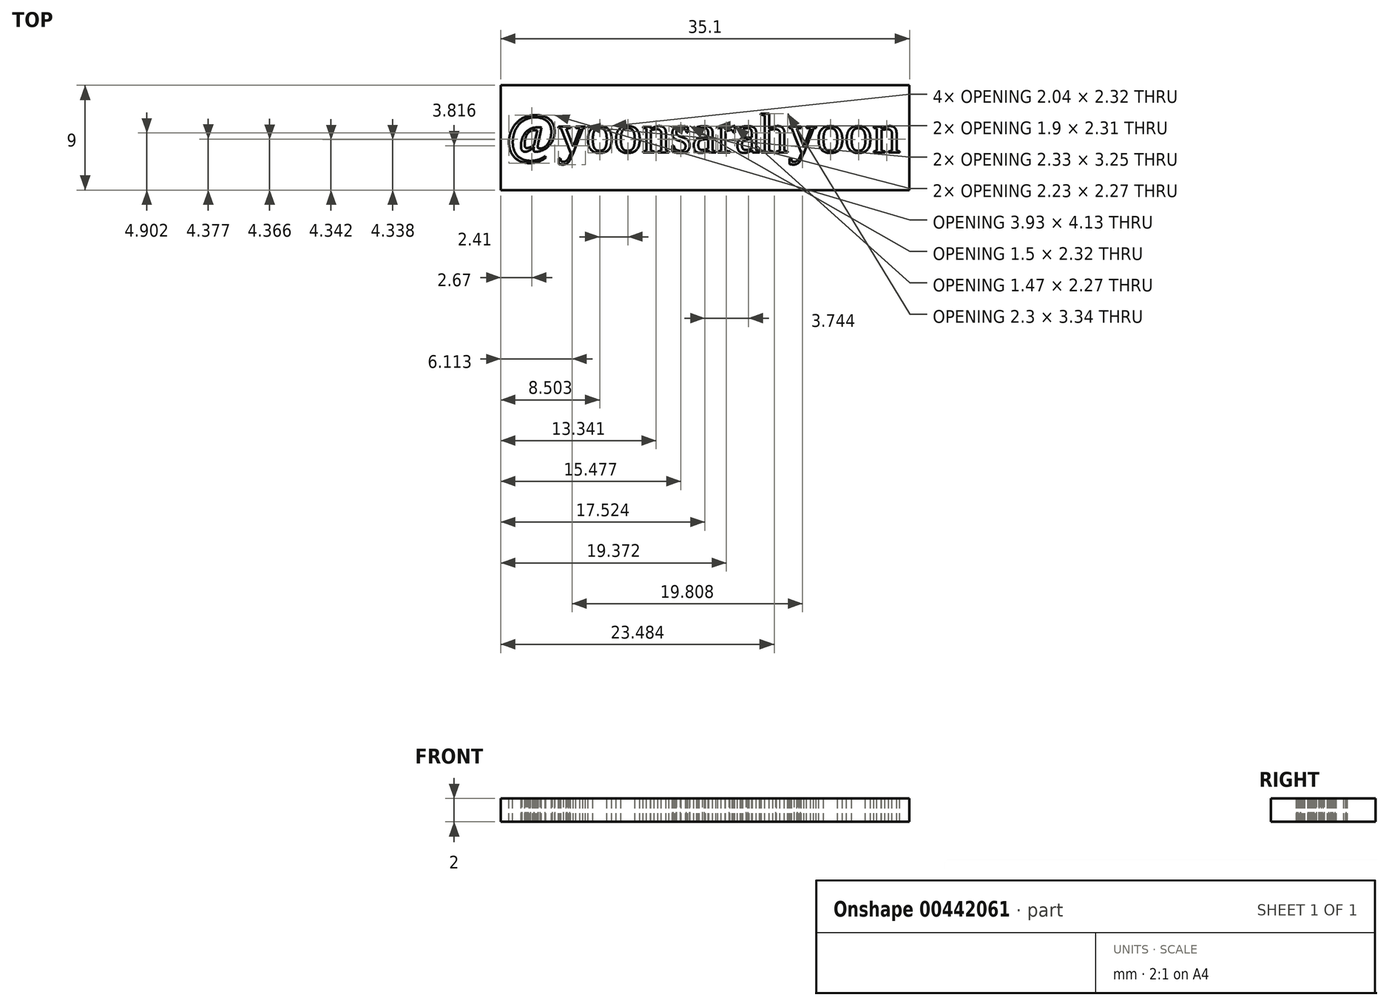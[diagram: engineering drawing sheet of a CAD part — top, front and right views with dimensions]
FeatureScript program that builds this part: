
annotation { "Feature Type Name" : "Feature", "Feature Type Description" : "" }
export const myFeature = defineFeature(function(context is Context, id is Id, definition is map)
    precondition{}
    {
        {
            var Q0;
            Q0=qCreatedBy(makeId("Top.planeOp"),FACE);
            var sketch = newSketch(context, id + "F0", { "sketchPlane" : qUnion([Q0])});
            skLineSegment(sketch, "E0.bottom", {"start": v(17.55, -4.5) * mm, "end": v(-17.55, -4.5) * mm});
            skLineSegment(sketch, "E0.top", {"start": v(17.55, 4.5) * mm, "end": v(-17.55, 4.5) * mm});
            skLineSegment(sketch, "E0.left", {"start": v(17.55, -4.5) * mm, "end": v(17.55, 4.5) * mm});
            skLineSegment(sketch, "E0.right", {"start": v(-17.55, -4.5) * mm, "end": v(-17.55, 4.5) * mm});
            skPoint(sketch, "E0.middle", {"position": v(0, 0) * mm});
            skSolve(sketch);
        }
        {
            var Q0;
            Q0=makeQuery(id+"F0.imprint","IMPRINT",FACE,{"disambiguationData":[TD([[makeQuery(id+"F0.imprint","IMPRINT",EDGE,{"derivedFrom":sQuery(id+"F0.wireOp",EDGE,"E0.bottom")}),-1.0]])]});
            extrude(context, id + "F1", {"entities" : qUnion([Q0]), "depth" : 2 * mm, "offsetDistance" : 25 * mm});
        }
        {
            var Q0;
            Q0=makeQuery(id+"F1.opExtrude","CAP_FACE",FACE,{"disambiguationData":[OSD([sQuery(id+"F0.wireOp",EDGE,"E0.bottom"),sQuery(id+"F0.wireOp",EDGE,"E0.top"),sQuery(id+"F0.wireOp",EDGE,"E0.left"),sQuery(id+"F0.wireOp",EDGE,"E0.right")])],"isStart":false});
            var sketch = newSketch(context, id + "F2", { "sketchPlane" : qUnion([Q0])});
            skText(sketch, "E1", { "text": "@yoonsarahyoon", "fontName": "Tinos-Regular.ttf"});
            const initialGuessF2  = {"E1": [-0.0171, -0.00127, 1, 0, 0.00347]};
            skSetInitialGuess(sketch, initialGuessF2);
            skSolve(sketch);
        }
        {
            var Q0;
            Q0 = qSketchRegion(id + "F2", true);
            extrude(context, id + "F3", {"entities" : qUnion([Q0]), "operationType" : NewBodyOperationType.REMOVE, "oppositeDirection" : true, "depth" : 2 * mm, "offsetDistance" : 25 * mm});
        }
    });
